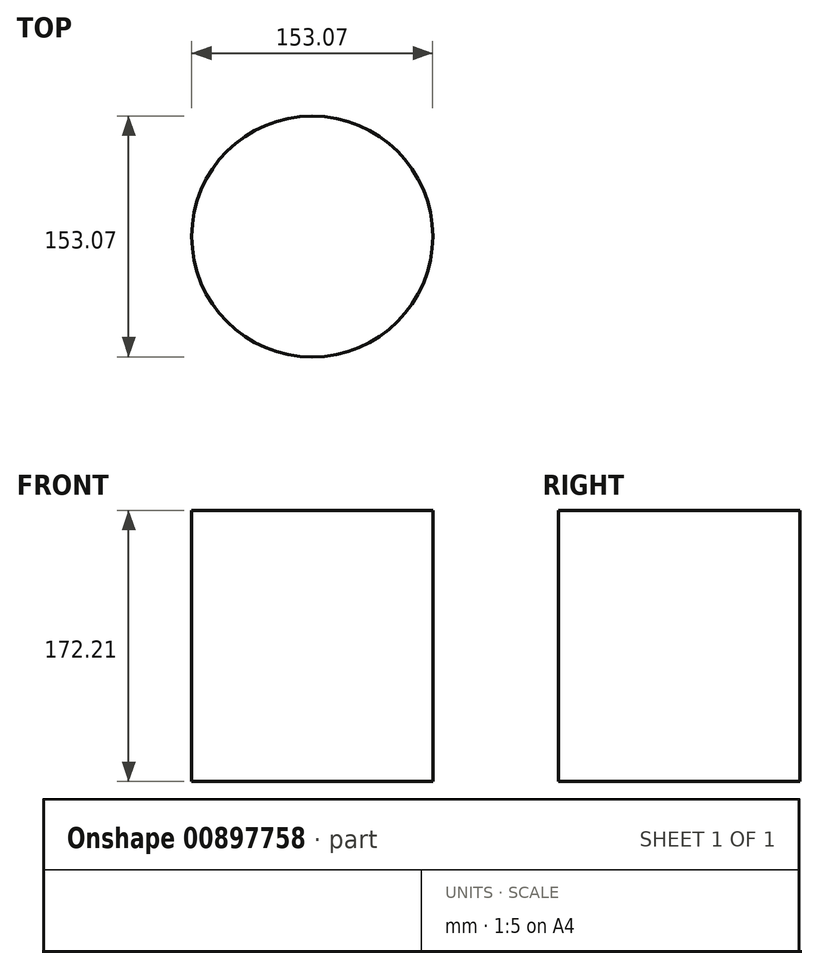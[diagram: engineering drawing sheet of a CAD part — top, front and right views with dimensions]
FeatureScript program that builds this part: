
annotation { "Feature Type Name" : "Feature", "Feature Type Description" : "" }
export const myFeature = defineFeature(function(context is Context, id is Id, definition is map)
    precondition{}
    {
        {
            var Q0;
            Q0=qCreatedBy(makeId("Top.planeOp"),FACE);
            var sketch = newSketch(context, id + "F0", { "sketchPlane" : qUnion([Q0])});
            skCircle(sketch, "E0", {"center": v(-27.57, 7.24) * mm, "radius": 76.54 * mm});
            skPoint(sketch, "E0.first.point", {"position": v(-92.94, 47.05) * mm});
            skPoint(sketch, "E0.second.point", {"position": v(40.88, -27) * mm});
            skPoint(sketch, "E0.third.point", {"position": v(-77.34, -50.91) * mm});
            skSolve(sketch);
        }
        {
            var Q0;
            Q0=makeQuery(id+"F0.imprint","IMPRINT",FACE,{"disambiguationData":[TD([[makeQuery(id+"F0.imprint","IMPRINT",EDGE,{"derivedFrom":sQuery(id+"F0.wireOp",EDGE,"E0")}),1.0]])]});
            extrude(context, id + "F1", {"entities" : qUnion([Q0]), "depth" : 172.21 * mm, "offsetDistance" : 25.4 * mm});
        }
    });
